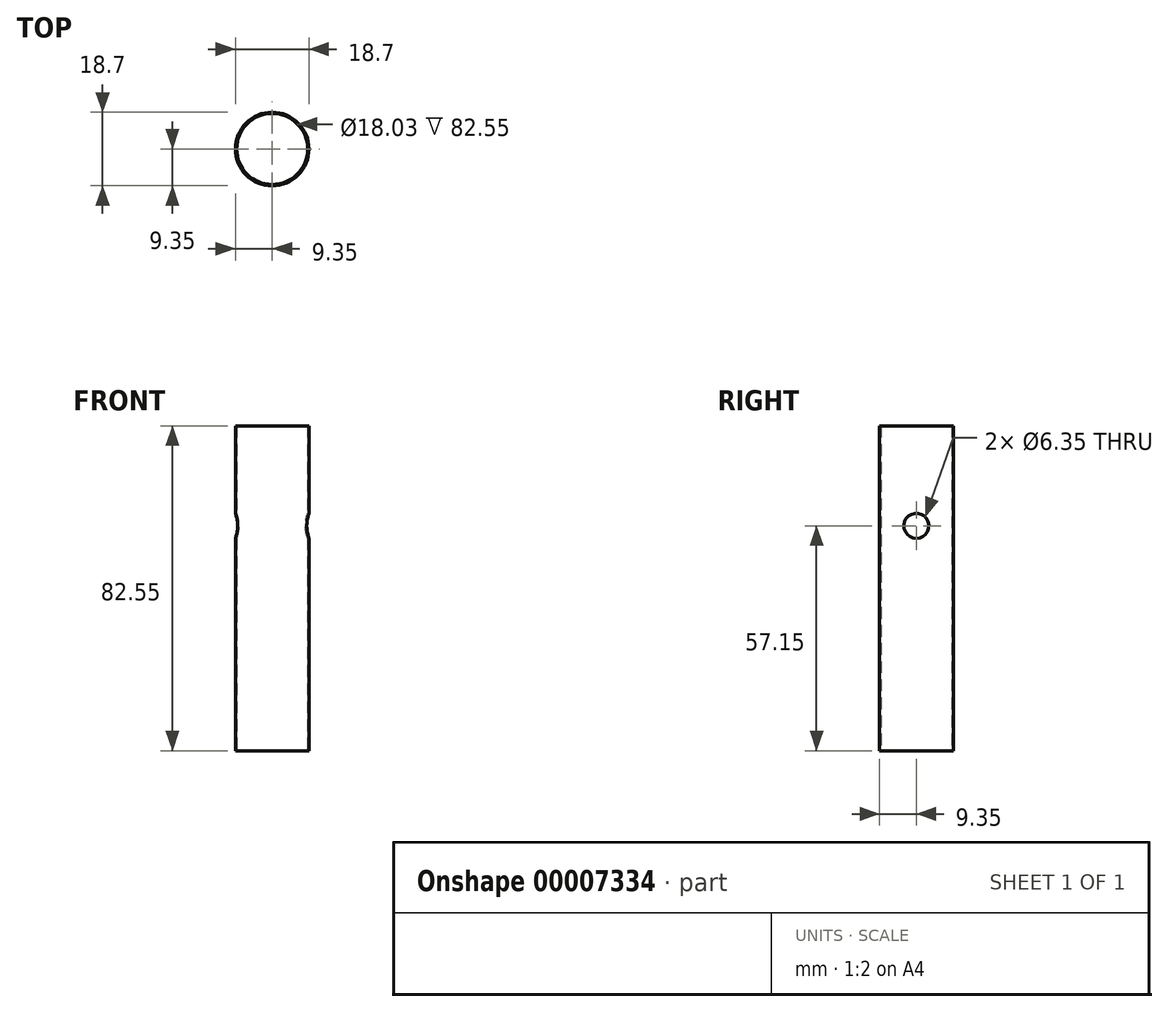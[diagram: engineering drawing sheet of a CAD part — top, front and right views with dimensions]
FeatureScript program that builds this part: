
annotation { "Feature Type Name" : "Feature", "Feature Type Description" : "" }
export const myFeature = defineFeature(function(context is Context, id is Id, definition is map)
    precondition{}
    {
        {
            var Q0;
            Q0=qCreatedBy(makeId("Front.planeOp"),FACE);
            var sketch = newSketch(context, id + "F0", { "sketchPlane" : qUnion([Q0])});
            skLineSegment(sketch, "E0.bottom", {"start": v(9.02, 0) * mm, "end": v(9.35, 0) * mm});
            skLineSegment(sketch, "E0.top", {"start": v(9.02, 82.55) * mm, "end": v(9.35, 82.55) * mm});
            skLineSegment(sketch, "E0.left", {"start": v(9.02, 0) * mm, "end": v(9.02, 82.55) * mm});
            skLineSegment(sketch, "E0.right", {"start": v(9.35, 0) * mm, "end": v(9.35, 82.55) * mm});
            skLineSegment(sketch, "E1", {"start": v(9.02, 0) * mm, "end": v(0, 0) * mm});
            skLineSegment(sketch, "E2", {"start": v(0, 0) * mm, "end": v(0, 82.55) * mm});
            skSolve(sketch);
        }
        {
            var Q0;
            Q0=qSketchRegion(id+"F0",true);
            var Q1;
            Q1=sQuery(id+"F0.wireOp",EDGE,"E2");
            revolve(context, id + "F1", {"entities" : qUnion([Q0]), "axis" : qUnion([Q1]), "revolveType" : RevolveType.FULL});
        }
        {
            var Q0;
            Q0=qCreatedBy(makeId("Top.planeOp"),FACE);
            var sketch = newSketch(context, id + "F2", { "sketchPlane" : qUnion([Q0])});
            skCircle(sketch, "E3.0", {"center": v(0, 0) * mm, "radius": 9.35 * mm});
            skCircle(sketch, "E4", {"center": v(0, 0) * mm, "radius": 63.5 * mm});
            skLineSegment(sketch, "E5", {"start": v(0, 0) * mm, "end": v(0, 63.5) * mm});
            skLineSegment(sketch, "E6", {"start": v(0, 0) * mm, "end": v(55, -31.75) * mm});
            skLineSegment(sketch, "E7", {"start": v(0, 0) * mm, "end": v(-55, -31.75) * mm});
            skPoint(sketch, "E8", {"position": v(0, 9.35) * mm});
            skPoint(sketch, "E9", {"position": v(8.1, -4.67) * mm});
            skPoint(sketch, "E10", {"position": v(-8.1, -4.67) * mm});
            skLineSegment(sketch, "E11", {"start": v(0, 0) * mm, "end": v(0.4, -0.69) * mm});
            skLineSegment(sketch, "E12", {"start": v(0.4, -0.69) * mm, "end": v(-54.6, -32.44) * mm});
            skLineSegment(sketch, "E13", {"start": v(-54.6, -32.44) * mm, "end": v(-55, -31.75) * mm});
            skCircle(sketch, "E14", {"center": v(-8.16, -8.13) * mm, "radius": 2.17 * mm});
            skSolve(sketch);
        }
        {
            var Q0;
            Q0=qCreatedBy(makeId("Top.planeOp"),FACE);
            var sketch = newSketch(context, id + "F3", { "sketchPlane" : qUnion([Q0])});
            skCircle(sketch, "E15.0", {"center": v(0, 0) * mm, "radius": 63.5 * mm});
            skCircle(sketch, "E16.0", {"center": v(0, 0) * mm, "radius": 9.35 * mm});
            skLineSegment(sketch, "E17.0", {"start": v(0, 0) * mm, "end": v(0, 63.5) * mm});
            skLineSegment(sketch, "E18", {"start": v(0, 0) * mm, "end": v(63.5, 0) * mm});
            skLineSegment(sketch, "E19", {"start": v(0, 0) * mm, "end": v(0, -63.5) * mm});
            skLineSegment(sketch, "E20", {"start": v(0, 0) * mm, "end": v(-63.5, 0) * mm});
            skPoint(sketch, "E21", {"position": v(0, 9.35) * mm});
            skPoint(sketch, "E22", {"position": v(9.35, 0) * mm});
            skPoint(sketch, "E23", {"position": v(0, -9.35) * mm});
            skPoint(sketch, "E24", {"position": v(-9.35, 0) * mm});
            skLineSegment(sketch, "E25", {"start": v(0, 0) * mm, "end": v(44.9, 44.9) * mm});
            skPoint(sketch, "E26", {"position": v(6.6, 6.6) * mm});
            skSolve(sketch);
        }
        {
            var Q0;
            Q0=qCreatedBy(makeId("Top.planeOp"),FACE);
            var sketch = newSketch(context, id + "F4", { "sketchPlane" : qUnion([Q0])});
            skCircle(sketch, "E27.0", {"center": v(0, 0) * mm, "radius": 63.5 * mm});
            skLineSegment(sketch, "E28.0", {"start": v(0, 0) * mm, "end": v(0, 63.5) * mm});
            skCircle(sketch, "E29.0", {"center": v(0, 0) * mm, "radius": 9.35 * mm});
            skLineSegment(sketch, "E30", {"start": v(0, 0) * mm, "end": v(60.4, 19.62) * mm});
            skLineSegment(sketch, "E31", {"start": v(0, 0) * mm, "end": v(37.32, -51.37) * mm});
            skLineSegment(sketch, "E32.0.MirrorCS", {"start": v(0, 0) * mm, "end": v(-60.4, 19.62) * mm});
            skLineSegment(sketch, "E33.0.MirrorCS", {"start": v(0, 0) * mm, "end": v(-37.32, -51.37) * mm});
            skPoint(sketch, "E34", {"position": v(0, 9.35) * mm});
            skPoint(sketch, "E35", {"position": v(8.89, 2.89) * mm});
            skPoint(sketch, "E36", {"position": v(-8.89, 2.89) * mm});
            skPoint(sketch, "E37", {"position": v(-5.5, -7.56) * mm});
            skPoint(sketch, "E38", {"position": v(5.5, -7.56) * mm});
            skSolve(sketch);
        }
        {
            var Q0;
            Q0=qCreatedBy(makeId("Right.planeOp"),FACE);
            var sketch = newSketch(context, id + "F5", { "sketchPlane" : qUnion([Q0])});
            skLineSegment(sketch, "E39", {"start": v(0, 0) * mm, "end": v(0, 82.55) * mm, "construction": true});
            skCircle(sketch, "E40", {"center": v(0, 57.15) * mm, "radius": 3.18 * mm});
            skSolve(sketch);
        }
        {
            var Q0;
            Q0 = qSketchRegion(id + "F5", true);
            extrude(context, id + "F6", {"entities" : qUnion([Q0]), "operationType" : NewBodyOperationType.REMOVE, "oppositeDirection" : true, "depth" : 76.2 * mm, "symmetric" : true});
        }
    });
